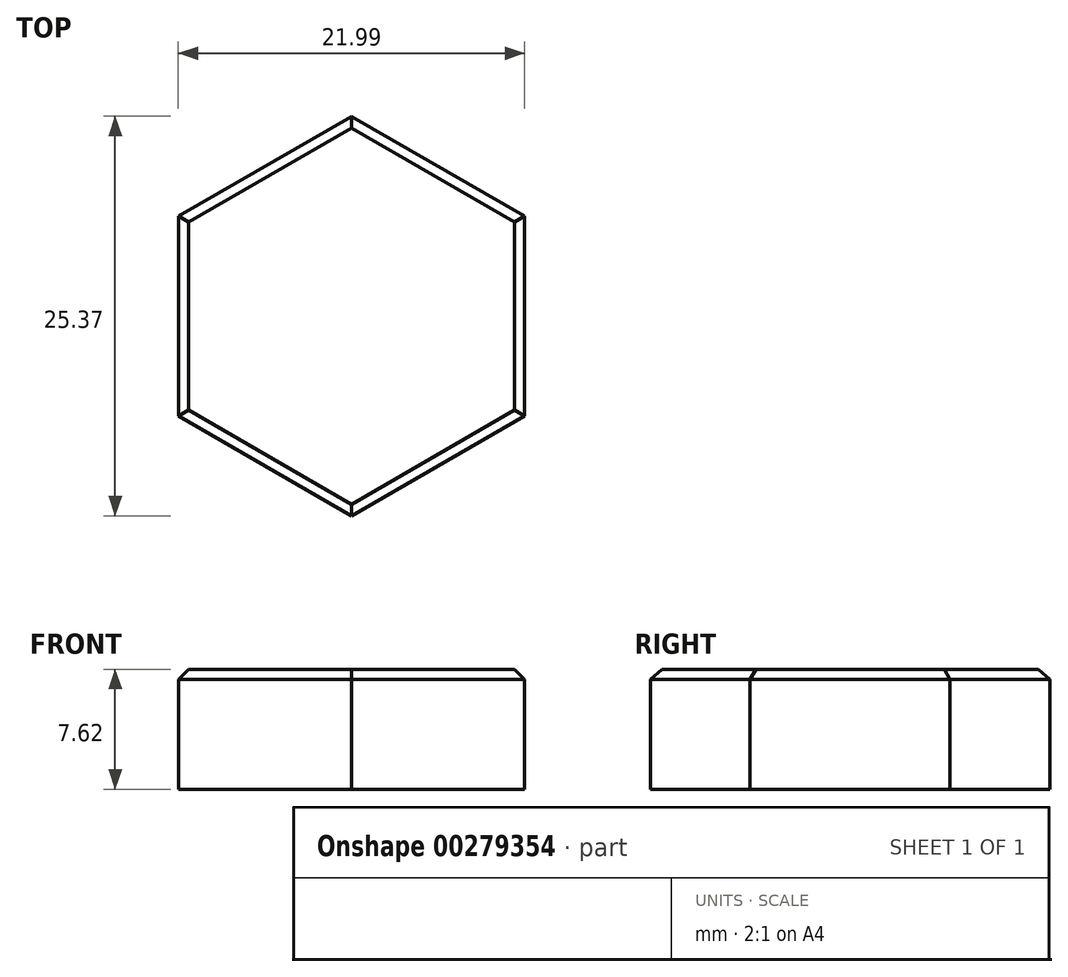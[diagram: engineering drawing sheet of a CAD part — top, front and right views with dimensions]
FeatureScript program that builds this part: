
annotation { "Feature Type Name" : "Feature", "Feature Type Description" : "" }
export const myFeature = defineFeature(function(context is Context, id is Id, definition is map)
    precondition{}
    {
        {
            var Q0;
            Q0=qCreatedBy(makeId("Top.planeOp"),FACE);
            var sketch = newSketch(context, id + "F0", { "sketchPlane" : qUnion([Q0])});
            skLineSegment(sketch, "E0.0", {"start": v(-0.01, 12.68) * mm, "end": v(10.98, 6.33) * mm});
            skLineSegment(sketch, "E0.1", {"start": v(10.98, 6.33) * mm, "end": v(10.98, -6.36) * mm});
            skLineSegment(sketch, "E0.2", {"start": v(10.98, -6.36) * mm, "end": v(0, -12.7) * mm});
            skLineSegment(sketch, "E0.3", {"start": v(0, -12.7) * mm, "end": v(-11, -6.35) * mm});
            skLineSegment(sketch, "E0.4", {"start": v(-11, -6.35) * mm, "end": v(-11, 6.34) * mm});
            skLineSegment(sketch, "E0.5", {"start": v(-11, 6.34) * mm, "end": v(-0.01, 12.68) * mm});
            skCircle(sketch, "E1", {"center": v(0, 0) * mm, "radius": 12.7 * mm, "construction": true});
            skSolve(sketch);
        }
        {
            var Q0;
            Q0=makeQuery(id+"F0.imprint","IMPRINT",FACE,{"disambiguationData":[TD([[makeQuery(id+"F0.imprint","IMPRINT",EDGE,{"derivedFrom":sQuery(id+"F0.wireOp",EDGE,"E0.0")}),-1.0]])]});
            var Q1;
            Q1=sQuery(id+"F0.wireOp",EDGE,"E0.5");
            var Q2;
            Q2=sQuery(id+"F0.wireOp",EDGE,"E0.0");
            var Q3;
            Q3=sQuery(id+"F0.wireOp",EDGE,"E0.1");
            var Q4;
            Q4=sQuery(id+"F0.wireOp",EDGE,"E0.2");
            var Q5;
            Q5=sQuery(id+"F0.wireOp",EDGE,"E0.3");
            var Q6;
            Q6=sQuery(id+"F0.wireOp",EDGE,"E0.4");
            extrude(context, id + "F1", {"entities" : qUnion([Q0]), "surfaceEntities" : qUnion([Q1, Q2, Q3, Q4, Q5, Q6]), "depth" : 7.62 * mm});
        }
        {
            var Q0;
            Q0=makeQuery(id+"F1.opExtrude","CAP_FACE",FACE,{"disambiguationData":[OSD([sQuery(id+"F0.wireOp",EDGE,"E0.0"),sQuery(id+"F0.wireOp",EDGE,"E0.1"),sQuery(id+"F0.wireOp",EDGE,"E0.2"),sQuery(id+"F0.wireOp",EDGE,"E0.3"),sQuery(id+"F0.wireOp",EDGE,"E0.4"),sQuery(id+"F0.wireOp",EDGE,"E0.5")])],"isStart":false});
            chamfer(context, id + "F2", {"entities" : qUnion([Q0]), "width" : 0.64 * mm, "tangentPropagation" : true});
        }
    });
